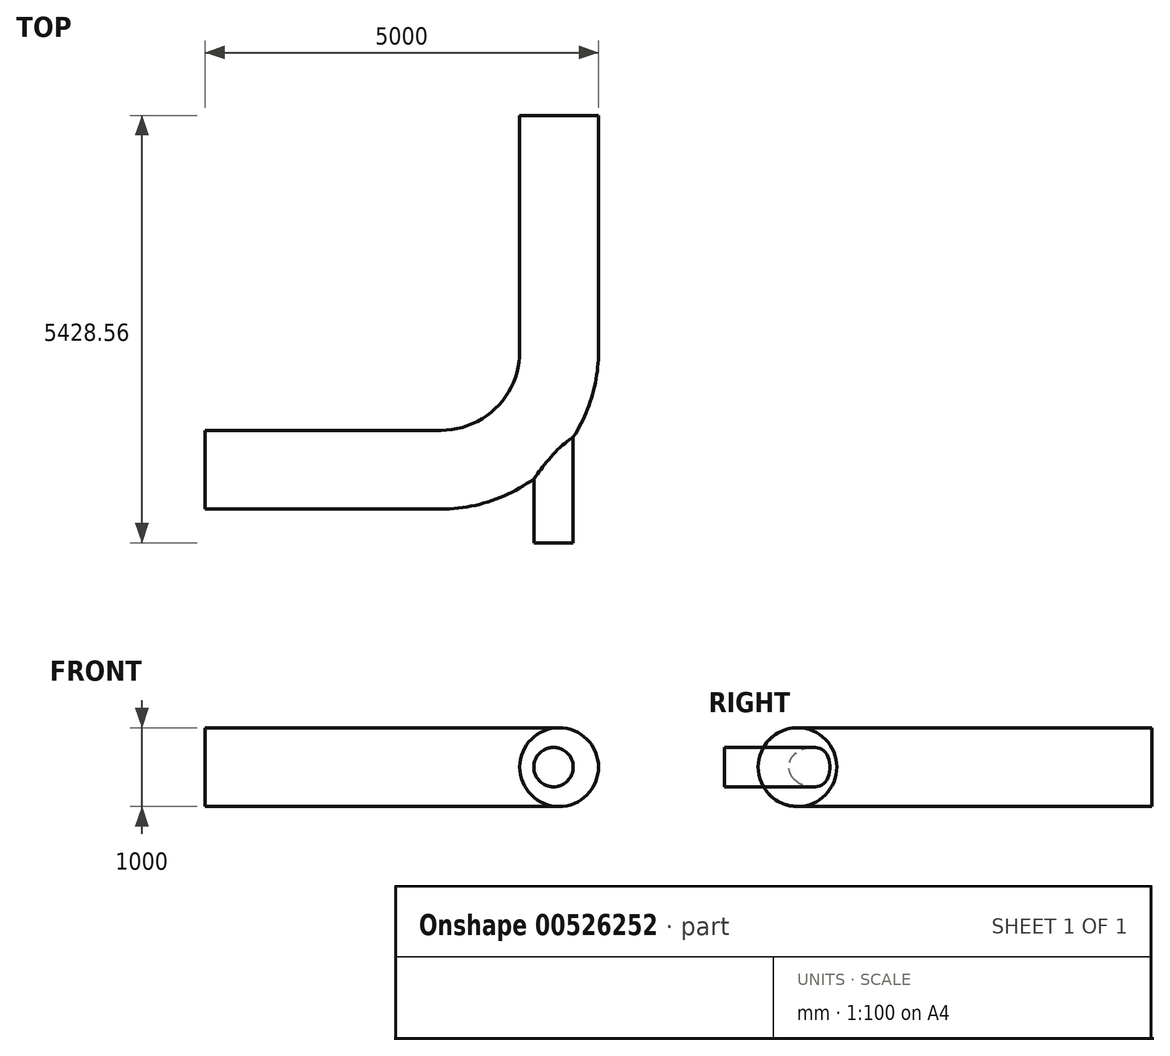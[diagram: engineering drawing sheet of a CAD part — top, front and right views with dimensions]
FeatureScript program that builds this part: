
annotation { "Feature Type Name" : "Feature", "Feature Type Description" : "" }
export const myFeature = defineFeature(function(context is Context, id is Id, definition is map)
    precondition{}
    {
        {
            var Q0;
            Q0=qCreatedBy(makeId("Top.planeOp"),FACE);
            var sketch = newSketch(context, id + "F0", { "sketchPlane" : qUnion([Q0])});
            skLineSegment(sketch, "E0", {"start": v(0, 0) * mm, "end": v(3000, 0) * mm});
            skArc(sketch, "E1", {"start": v(3000, 0) * mm, "mid": v(4060.66, 439.34) * mm, "end": v(4500, 1500) * mm});
            skLineSegment(sketch, "E2", {"start": v(4500, 1500) * mm, "end": v(4500, 4500) * mm});
            skArc(sketch, "E3.0", {"start": v(3000, -528.83) * mm, "mid": v(4414.21, 56.95) * mm, "end": v(5000, 1471.17) * mm});
            skLineSegment(sketch, "E4", {"start": v(3000, 1500) * mm, "end": v(4428.56, 71.44) * mm});
            skLineSegment(sketch, "E5", {"start": v(3000, 1500) * mm, "end": v(3812.97, 1500) * mm});
            skLineSegment(sketch, "E6", {"start": v(4428.56, 71.44) * mm, "end": v(4428.56, -928.56) * mm});
            skSolve(sketch);
        }
        {
            var Q0;
            Q0=qCreatedBy(makeId("Right.planeOp"),FACE);
            var sketch = newSketch(context, id + "F1", { "sketchPlane" : qUnion([Q0])});
            skCircle(sketch, "E7", {"center": v(0, 0) * mm, "radius": 500 * mm});
            skSolve(sketch);
        }
        {
            var Q0;
            Q0=makeQuery(id+"F1.imprint","IMPRINT",FACE,{"disambiguationData":[TD([[makeQuery(id+"F1.imprint","IMPRINT",EDGE,{"derivedFrom":sQuery(id+"F1.wireOp",EDGE,"E7")}),1.0]])]});
            var Q1;
            Q1=sQuery(id+"F0.wireOp",EDGE,"E0");
            var Q2;
            Q2=sQuery(id+"F0.wireOp",EDGE,"E1");
            var Q3;
            Q3=sQuery(id+"F0.wireOp",EDGE,"E2");
            sweep(context, id + "F2", {"profiles" : qUnion([Q0]), "path" : qUnion([Q1, Q2, Q3])});
        }
        {
            var Q0;
            Q0=sQuery(id+"F0.wireOp",VERTEX,"E6.end");
            var Q1;
            Q1=sQuery(id+"F0.wireOp",EDGE,"E6");
            cPlane(context, id + "F3", {"entities" : qUnion([Q0, Q1]), "cplaneType" : CPlaneType.LINE_POINT, "offset" : 25 * mm, "width" : 150 * mm, "height" : 150 * mm});
        }
        {
            var Q0;
            Q0=qCreatedBy(id+"F3.planeOp",FACE);
            var sketch = newSketch(context, id + "F4", { "sketchPlane" : qUnion([Q0])});
            skPoint(sketch, "E8.0", {"position": v(4428.56, 0) * mm});
            skCircle(sketch, "E9", {"center": v(4428.56, 0) * mm, "radius": 250 * mm});
            skSolve(sketch);
        }
        {
            var Q0;
            Q0=makeQuery(id+"F4.imprint","IMPRINT",FACE,{"disambiguationData":[TD([[makeQuery(id+"F4.imprint","IMPRINT",EDGE,{"derivedFrom":sQuery(id+"F4.wireOp",EDGE,"E9")}),1.0]])]});
            var Q1;
            Q1=sQuery(id+"F4.wireOp",EDGE,"E9");
            var Q2;
            Q2=makeQuery(id+"F2.opSweep","CAP_FACE",FACE,{"disambiguationData":[OSD([sQuery(id+"F0.wireOp",VERTEX,"E2.end"),sQuery(id+"F1.wireOp",EDGE,"E7")])],"isStart":false});
            extrude(context, id + "F5", {"entities" : qUnion([Q0]), "operationType" : NewBodyOperationType.ADD, "surfaceEntities" : qUnion([Q1]), "endBound" : BoundingType.UP_TO_SURFACE, "oppositeDirection" : true, "depth" : 1790 * mm, "endBoundEntityFace" : qUnion([Q2]), "offsetDistance" : 25 * mm});
        }
    });
